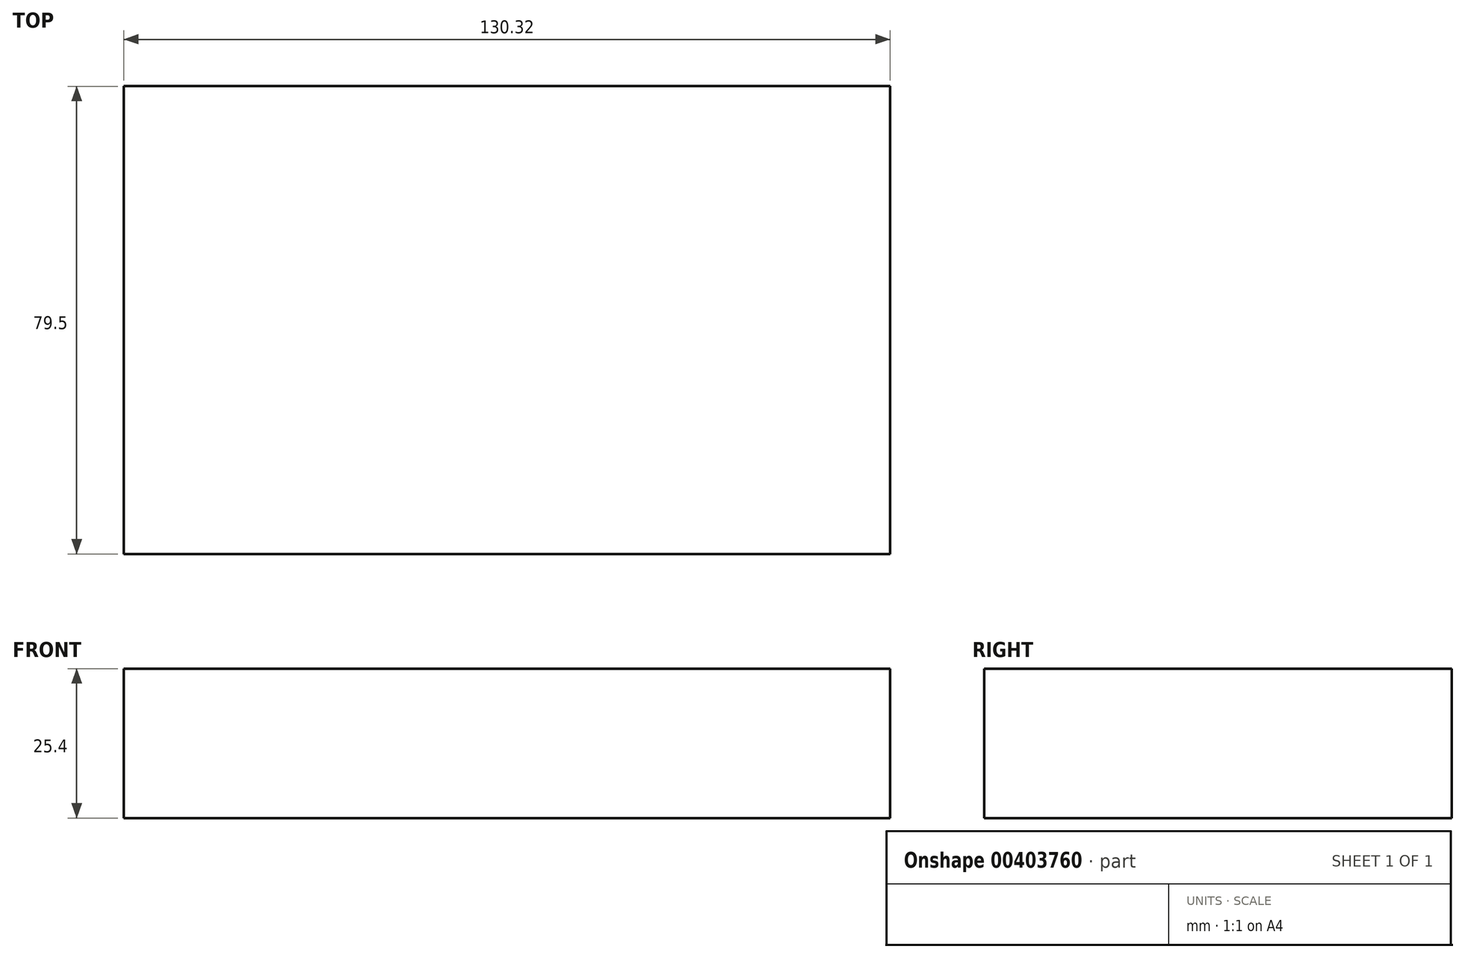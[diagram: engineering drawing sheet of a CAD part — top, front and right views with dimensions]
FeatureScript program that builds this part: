
annotation { "Feature Type Name" : "Feature", "Feature Type Description" : "" }
export const myFeature = defineFeature(function(context is Context, id is Id, definition is map)
    precondition{}
    {
        {
            var Q0;
            Q0=qCreatedBy(makeId("Top.planeOp"),FACE);
            var sketch = newSketch(context, id + "F0", { "sketchPlane" : qUnion([Q0])});
            skLineSegment(sketch, "E0.bottom", {"start": v(-65.16, 39.75) * mm, "end": v(65.16, 39.75) * mm});
            skLineSegment(sketch, "E0.top", {"start": v(-65.16, -39.75) * mm, "end": v(65.16, -39.75) * mm});
            skLineSegment(sketch, "E0.left", {"start": v(-65.16, 39.75) * mm, "end": v(-65.16, -39.75) * mm});
            skLineSegment(sketch, "E0.right", {"start": v(65.16, 39.75) * mm, "end": v(65.16, -39.75) * mm});
            skPoint(sketch, "E0.middle", {"position": v(0, 0) * mm});
            skSolve(sketch);
        }
        {
            var Q0;
            Q0 = qSketchRegion(id + "F0", true);
            extrude(context, id + "F1", {"entities" : qUnion([Q0]), "depth" : 25.4 * mm, "offsetDistance" : 25.4 * mm});
        }
    });
